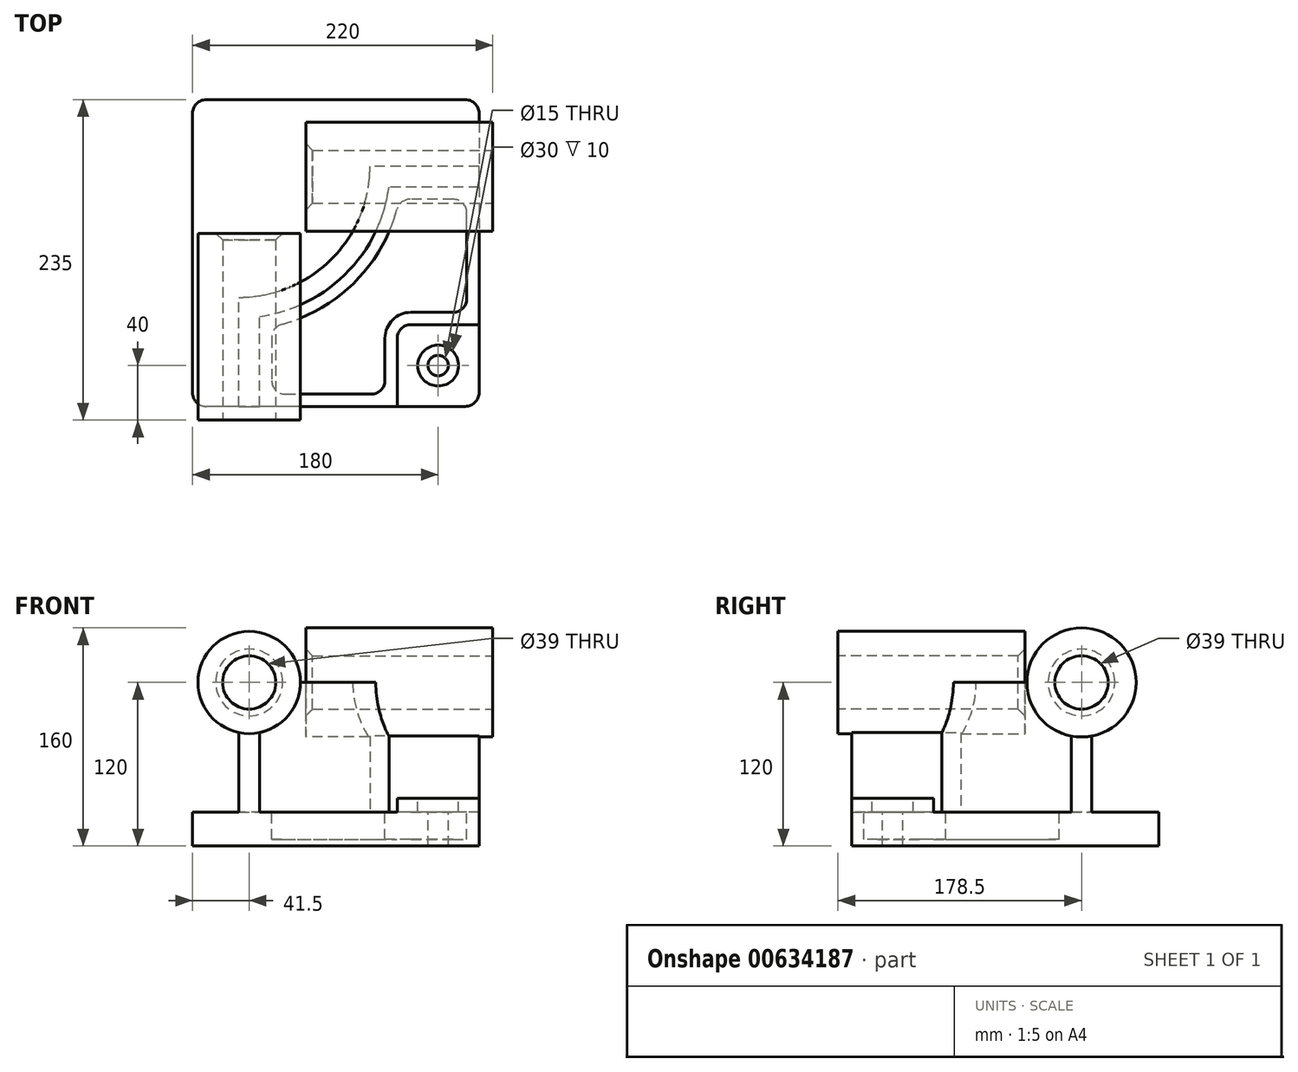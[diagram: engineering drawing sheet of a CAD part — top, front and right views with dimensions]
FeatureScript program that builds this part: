
annotation { "Feature Type Name" : "Feature", "Feature Type Description" : "" }
export const myFeature = defineFeature(function(context is Context, id is Id, definition is map)
    precondition{}
    {
        {
            var Q0;
            Q0=qCreatedBy(makeId("Top.planeOp"),FACE);
            var sketch = newSketch(context, id + "F0", { "sketchPlane" : qUnion([Q0])});
            skLineSegment(sketch, "E0.bottom", {"start": v(105, 112.5) * mm, "end": v(-105, 112.5) * mm});
            skLineSegment(sketch, "E0.top", {"start": v(105, -112.5) * mm, "end": v(-105, -112.5) * mm});
            skLineSegment(sketch, "E0.left", {"start": v(105, 112.5) * mm, "end": v(105, -112.5) * mm});
            skLineSegment(sketch, "E0.right", {"start": v(-105, 112.5) * mm, "end": v(-105, -112.5) * mm});
            skPoint(sketch, "E0.middle", {"position": v(0, 0) * mm});
            skSolve(sketch);
        }
        {
            var Q0;
            Q0=makeQuery(id+"F0.imprint","IMPRINT",FACE,{"disambiguationData":[TD([[makeQuery(id+"F0.imprint","IMPRINT",EDGE,{"derivedFrom":sQuery(id+"F0.wireOp",EDGE,"E0.bottom")}),1.0]])]});
            extrude(context, id + "F1", {"entities" : qUnion([Q0]), "depth" : 25 * mm, "offsetDistance" : 25 * mm});
        }
        {
            var Q0;
            Q0=makeQuery(id+"F1.opExtrude","CAP_FACE",FACE,{"disambiguationData":[OSD([sQuery(id+"F0.wireOp",EDGE,"E0.bottom"),sQuery(id+"F0.wireOp",EDGE,"E0.top"),sQuery(id+"F0.wireOp",EDGE,"E0.left"),sQuery(id+"F0.wireOp",EDGE,"E0.right")])],"isStart":false});
            var sketch = newSketch(context, id + "F2", { "sketchPlane" : qUnion([Q0])});
            skLineSegment(sketch, "E1", {"start": v(-71, -112.5) * mm, "end": v(-71, -32.5) * mm});
            skLineSegment(sketch, "E2", {"start": v(105, 63.5) * mm, "end": v(25, 63.5) * mm});
            skArc(sketch, "E3", {"start": v(-71, -32.5) * mm, "mid": v(-3.12, -4.38) * mm, "end": v(25, 63.5) * mm});
            skLineSegment(sketch, "E4", {"start": v(-71, 63.5) * mm, "end": v(25, 63.5) * mm, "construction": true});
            skLineSegment(sketch, "E5", {"start": v(-71, 63.5) * mm, "end": v(-71, -32.5) * mm, "construction": true});
            skLineSegment(sketch, "E6.0", {"start": v(-56, -112.5) * mm, "end": v(-56, -46.48) * mm});
            skArc(sketch, "E6.1", {"start": v(-56, -46.48) * mm, "mid": v(7.49, -14.99) * mm, "end": v(38.98, 48.5) * mm});
            skLineSegment(sketch, "E6.2", {"start": v(105, 48.5) * mm, "end": v(38.98, 48.5) * mm});
            skSolve(sketch);
        }
        {
            var Q0;
            {var subQ4=sQuery(id+"F2.wireOp",EDGE,"E1");Q0=makeQuery(id+"F2.imprint","IMPRINT",FACE,{"disambiguationData":[TD([[makeQuery(id+"F2.imprint","IMPRINT",EDGE,{"derivedFrom":subQ4}),-1.0]])]});}
            extrude(context, id + "F3", {"entities" : qUnion([Q0]), "operationType" : NewBodyOperationType.ADD, "depth" : 95 * mm, "offsetDistance" : 25 * mm});
        }
        {
            var Q0;
            {var subQ0=sQuery(id+"F0.wireOp",EDGE,"E0.top");Q0=makeQuery(id+"F3.boolean.opBoolean","MERGE",FACE,{"derivedFrom":[makeQuery(id+"F1.opExtrude","SWEPT_FACE",FACE,{"disambiguationData":[OSD([subQ0])]}),makeQuery(id+"F3.opExtrude","SWEPT_FACE",FACE,{"disambiguationData":[OSD([subQ0])]})]});}
            var sketch = newSketch(context, id + "F4", { "sketchPlane" : qUnion([Q0])});
            skCircle(sketch, "E7", {"center": v(-63.5, 120) * mm, "radius": 37.5 * mm});
            skSolve(sketch);
        }
        {
            var Q0;
            Q0 = qSketchRegion(id + "F4", true);
            extrude(context, id + "F5", {"entities" : qUnion([Q0]), "operationType" : NewBodyOperationType.ADD, "depth" : 10 * mm, "offsetDistance" : 25 * mm, "hasSecondDirection" : true, "secondDirectionOppositeDirection" : true, "secondDirectionDepth" : (137 - 10) * mm});
        }
        {
            var Q0;
            {var subQ0=sQuery(id+"F0.wireOp",EDGE,"E0.left");Q0=makeQuery(id+"F3.boolean.opBoolean","MERGE",FACE,{"derivedFrom":[makeQuery(id+"F1.opExtrude","SWEPT_FACE",FACE,{"disambiguationData":[OSD([subQ0])]}),makeQuery(id+"F3.opExtrude","SWEPT_FACE",FACE,{"disambiguationData":[OSD([subQ0])]})]});}
            var sketch = newSketch(context, id + "F6", { "sketchPlane" : qUnion([Q0])});
            skCircle(sketch, "E8", {"center": v(56, 120) * mm, "radius": 40 * mm});
            skSolve(sketch);
        }
        {
            var Q0;
            Q0 = qSketchRegion(id + "F6", true);
            extrude(context, id + "F7", {"entities" : qUnion([Q0]), "operationType" : NewBodyOperationType.ADD, "depth" : 10 * mm, "offsetDistance" : 25 * mm, "hasSecondDirection" : true, "secondDirectionOppositeDirection" : true, "secondDirectionDepth" : (137 - 10) * mm});
        }
        {
            var Q0;
            {var subQ0=sQuery(id+"F0.wireOp",EDGE,"E0.left");var subQ1=sQuery(id+"F0.wireOp",EDGE,"E0.top");Q0=makeQuery(id+"F3.boolean.opBoolean","SPLIT",FACE,{"disambiguationData":[TD([makeQuery(id+"F3.opExtrude","SWEPT_FACE",FACE,{"disambiguationData":[OSD([sQuery(id+"F2.wireOp",EDGE,"E6.0")])]})])],"derivedFrom":makeQuery(id+"F1.opExtrude","CAP_FACE",FACE,{"disambiguationData":[OSD([sQuery(id+"F0.wireOp",EDGE,"E0.bottom"),subQ1,subQ0,sQuery(id+"F0.wireOp",EDGE,"E0.right")])],"isStart":false})});}
            var sketch = newSketch(context, id + "F8", { "sketchPlane" : qUnion([Q0])});
            skLineSegment(sketch, "E9.bottom", {"start": v(105, -112.5) * mm, "end": v(45, -112.5) * mm});
            skLineSegment(sketch, "E9.top", {"start": v(105, -52.5) * mm, "end": v(45, -52.5) * mm});
            skLineSegment(sketch, "E9.left", {"start": v(105, -112.5) * mm, "end": v(105, -52.5) * mm});
            skLineSegment(sketch, "E9.right", {"start": v(45, -112.5) * mm, "end": v(45, -52.5) * mm});
            skSolve(sketch);
        }
        {
            var Q0;
            Q0 = qSketchRegion(id + "F8", true);
            extrude(context, id + "F9", {"entities" : qUnion([Q0]), "operationType" : NewBodyOperationType.ADD, "depth" : 10 * mm, "offsetDistance" : 25 * mm});
        }
        {
            var Q0;
            Q0=makeQuery(id+"F9.opExtrude","SWEPT_EDGE",EDGE,{"disambiguationData":[OSD([sQuery(id+"F8.wireOp",EDGE,"E9.top"),sQuery(id+"F8.wireOp",EDGE,"E9.right")])]});
            fillet(context, id + "F10", {"entities" : qUnion([Q0]), "radius" : 10 * mm, "tangentPropagation" : true, "allowEdgeOverflow" : false});
        }
        {
            var Q0;
            {var subQ0=sQuery(id+"F0.wireOp",EDGE,"E0.left");var subQ1=sQuery(id+"F0.wireOp",EDGE,"E0.top");Q0=makeQuery(id+"F3.boolean.opBoolean","SPLIT",FACE,{"disambiguationData":[TD([makeQuery(id+"F3.opExtrude","SWEPT_FACE",FACE,{"disambiguationData":[OSD([sQuery(id+"F2.wireOp",EDGE,"E6.0")])]})])],"derivedFrom":makeQuery(id+"F1.opExtrude","CAP_FACE",FACE,{"disambiguationData":[OSD([sQuery(id+"F0.wireOp",EDGE,"E0.bottom"),subQ1,subQ0,sQuery(id+"F0.wireOp",EDGE,"E0.right")])],"isStart":false})});}
            var sketch = newSketch(context, id + "F11", { "sketchPlane" : qUnion([Q0])});
            skLineSegment(sketch, "E10.0", {"start": v(-47, -54.08) * mm, "end": v(-47, -103.5) * mm});
            skArc(sketch, "E10.1", {"start": v(46.58, 39.5) * mm, "mid": v(13.85, -21.35) * mm, "end": v(-47, -54.08) * mm});
            skLineSegment(sketch, "E10.2", {"start": v(-47, -103.5) * mm, "end": v(36, -103.5) * mm});
            skLineSegment(sketch, "E10.3", {"start": v(96, 39.5) * mm, "end": v(46.58, 39.5) * mm});
            skLineSegment(sketch, "E10.4", {"start": v(36, -103.5) * mm, "end": v(36, -62.5) * mm});
            skArc(sketch, "E10.5", {"start": v(36, -62.5) * mm, "mid": v(41.56, -49.06) * mm, "end": v(55, -43.5) * mm});
            skLineSegment(sketch, "E10.6", {"start": v(55, -43.5) * mm, "end": v(96, -43.5) * mm});
            skLineSegment(sketch, "E10.7", {"start": v(96, -43.5) * mm, "end": v(96, 39.5) * mm});
            skSolve(sketch);
        }
        {
            var Q0;
            Q0 = qSketchRegion(id + "F11", true);
            extrude(context, id + "F12", {"entities" : qUnion([Q0]), "operationType" : NewBodyOperationType.REMOVE, "oppositeDirection" : true, "depth" : (25 - 5) * mm, "offsetDistance" : 25 * mm});
        }
        {
            var Q0;
            Q0=makeQuery(id+"F9.opExtrude","CAP_FACE",FACE,{"disambiguationData":[OSD([sQuery(id+"F8.wireOp",EDGE,"E9.bottom"),sQuery(id+"F8.wireOp",EDGE,"E9.top"),sQuery(id+"F8.wireOp",EDGE,"E9.left"),sQuery(id+"F8.wireOp",EDGE,"E9.right")])],"isStart":false});
            var sketch = newSketch(context, id + "F13", { "sketchPlane" : qUnion([Q0])});
            skCircle(sketch, "E11", {"center": v(75, -82.5) * mm, "radius": 15 * mm});
            skSolve(sketch);
        }
        {
            var Q0;
            Q0=sQuery(id+"F13.wireOp",VERTEX,"E11.center");
            var Q1;
            Q1=makeQuery(id+"F1.opExtrude","SWEPT_BODY",BODY,{"disambiguationData":[OSD([sQuery(id+"F0.wireOp",EDGE,"E0.bottom"),sQuery(id+"F0.wireOp",EDGE,"E0.top"),sQuery(id+"F0.wireOp",EDGE,"E0.left"),sQuery(id+"F0.wireOp",EDGE,"E0.right")])]});
            hole(context, id + "F14", {"style" : HoleStyle.C_BORE, "endStyle" : HoleEndStyle.THROUGH, "holeDiameter" : 15 * mm, "cBoreDiameter" : 30 * mm, "cBoreDepth" : 10 * mm, "majorDiameter" : 6.35 * mm, "isTappedThrough" : true, "tappedDepth" : 12 * mm, "tapClearance" : 3, "locations" : qUnion([Q0]), "scope" : qUnion([Q1])});
        }
        {
            var Q0;
            Q0=makeQuery(id+"F12.boolean.opBoolean","COPY",EDGE,{"derivedFrom":makeQuery(id+"F12.opExtrude","SWEPT_EDGE",EDGE,{"disambiguationData":[OSD([sQuery(id+"F11.wireOp",EDGE,"E10.0"),sQuery(id+"F11.wireOp",EDGE,"E10.1")])]})});
            var Q1;
            Q1=makeQuery(id+"F12.boolean.opBoolean","COPY",EDGE,{"derivedFrom":makeQuery(id+"F12.opExtrude","SWEPT_EDGE",EDGE,{"disambiguationData":[OSD([sQuery(id+"F11.wireOp",EDGE,"E10.1"),sQuery(id+"F11.wireOp",EDGE,"E10.3")])]})});
            var Q2;
            Q2=makeQuery(id+"F12.boolean.opBoolean","COPY",EDGE,{"derivedFrom":makeQuery(id+"F12.opExtrude","SWEPT_EDGE",EDGE,{"disambiguationData":[OSD([sQuery(id+"F11.wireOp",EDGE,"E10.3"),sQuery(id+"F11.wireOp",EDGE,"E10.7")])]})});
            var Q3;
            Q3=makeQuery(id+"F12.boolean.opBoolean","COPY",EDGE,{"derivedFrom":makeQuery(id+"F12.opExtrude","SWEPT_EDGE",EDGE,{"disambiguationData":[OSD([sQuery(id+"F11.wireOp",EDGE,"E10.6"),sQuery(id+"F11.wireOp",EDGE,"E10.7")])]})});
            var Q4;
            Q4=makeQuery(id+"F12.boolean.opBoolean","COPY",EDGE,{"derivedFrom":makeQuery(id+"F12.opExtrude","SWEPT_EDGE",EDGE,{"disambiguationData":[OSD([sQuery(id+"F11.wireOp",EDGE,"E10.2"),sQuery(id+"F11.wireOp",EDGE,"E10.4")])]})});
            var Q5;
            Q5=makeQuery(id+"F12.boolean.opBoolean","COPY",EDGE,{"derivedFrom":makeQuery(id+"F12.opExtrude","SWEPT_EDGE",EDGE,{"disambiguationData":[OSD([sQuery(id+"F11.wireOp",EDGE,"E10.0"),sQuery(id+"F11.wireOp",EDGE,"E10.2")])]})});
            fillet(context, id + "F15", {"entities" : qUnion([Q0, Q1, Q2, Q3, Q4, Q5]), "radius" : 10 * mm, "tangentPropagation" : true, "allowEdgeOverflow" : false});
        }
        {
            var Q0;
            Q0=makeQuery(id+"F5.opExtrude","CAP_FACE",FACE,{"disambiguationData":[OSD([sQuery(id+"F4.wireOp",EDGE,"E7")])],"isStart":false});
            var sketch = newSketch(context, id + "F16", { "sketchPlane" : qUnion([Q0])});
            skCircle(sketch, "E12", {"center": v(-63.5, 120) * mm, "radius": 19.5 * mm});
            skSolve(sketch);
        }
        {
            var Q0;
            Q0 = qSketchRegion(id + "F16", true);
            extrude(context, id + "F17", {"entities" : qUnion([Q0]), "operationType" : NewBodyOperationType.REMOVE, "endBound" : BoundingType.THROUGH_ALL, "oppositeDirection" : true, "depth" : 25 * mm, "offsetDistance" : 25 * mm});
        }
        {
            var Q0;
            Q0=makeQuery(id+"F7.opExtrude","CAP_FACE",FACE,{"disambiguationData":[OSD([sQuery(id+"F6.wireOp",EDGE,"E8")])],"isStart":false});
            var sketch = newSketch(context, id + "F18", { "sketchPlane" : qUnion([Q0])});
            skCircle(sketch, "E13", {"center": v(56, 120) * mm, "radius": 19.5 * mm});
            skSolve(sketch);
        }
        {
            var Q0;
            Q0 = qSketchRegion(id + "F18", true);
            extrude(context, id + "F19", {"entities" : qUnion([Q0]), "operationType" : NewBodyOperationType.REMOVE, "endBound" : BoundingType.THROUGH_ALL, "oppositeDirection" : true, "depth" : 25 * mm, "offsetDistance" : 25 * mm});
        }
        {
            var Q0;
            Q0=makeQuery(id+"F19.boolean.opBoolean","COPY",EDGE,{"derivedFrom":makeQuery(id+"F19.opExtrude","CAP_EDGE",EDGE,{"disambiguationData":[OSD([sQuery(id+"F18.wireOp",EDGE,"E13")])],"isStart":true})});
            var Q1;
            Q1=makeQuery(id+"F19.boolean.opBoolean","INTERSECT",EDGE,{"derivedFrom":[makeQuery(id+"F7.opExtrude","CAP_FACE",FACE,{"disambiguationData":[OSD([sQuery(id+"F6.wireOp",EDGE,"E8")])],"isStart":true}),makeQuery(id+"F19.opExtrude","SWEPT_FACE",FACE,{"disambiguationData":[OSD([sQuery(id+"F18.wireOp",EDGE,"E13")])]})]});
            var Q2;
            Q2=makeQuery(id+"F17.boolean.opBoolean","INTERSECT",EDGE,{"derivedFrom":[makeQuery(id+"F5.opExtrude","CAP_FACE",FACE,{"disambiguationData":[OSD([sQuery(id+"F4.wireOp",EDGE,"E7")])],"isStart":true}),makeQuery(id+"F17.opExtrude","SWEPT_FACE",FACE,{"disambiguationData":[OSD([sQuery(id+"F16.wireOp",EDGE,"E12")])]})]});
            var Q3;
            Q3=makeQuery(id+"F17.boolean.opBoolean","COPY",EDGE,{"derivedFrom":makeQuery(id+"F17.opExtrude","CAP_EDGE",EDGE,{"disambiguationData":[OSD([sQuery(id+"F16.wireOp",EDGE,"E12")])],"isStart":true})});
            chamfer(context, id + "F20", {"entities" : qUnion([Q0, Q1, Q2, Q3]), "width" : 5 * mm, "tangentPropagation" : true});
        }
        {
            var Q0;
            Q0=makeQuery(id+"F1.opExtrude","SWEPT_EDGE",EDGE,{"disambiguationData":[OSD([sQuery(id+"F0.wireOp",EDGE,"E0.top"),sQuery(id+"F0.wireOp",EDGE,"E0.right")])]});
            var Q1;
            Q1=makeQuery(id+"F9.boolean.opBoolean","MERGE",EDGE,{"derivedFrom":[makeQuery(id+"F1.opExtrude","SWEPT_EDGE",EDGE,{"disambiguationData":[OSD([sQuery(id+"F0.wireOp",EDGE,"E0.top"),sQuery(id+"F0.wireOp",EDGE,"E0.left")])]}),makeQuery(id+"F9.opExtrude","SWEPT_EDGE",EDGE,{"disambiguationData":[OSD([sQuery(id+"F8.wireOp",EDGE,"E9.bottom"),sQuery(id+"F8.wireOp",EDGE,"E9.left")])]})]});
            var Q2;
            Q2=makeQuery(id+"F1.opExtrude","SWEPT_EDGE",EDGE,{"disambiguationData":[OSD([sQuery(id+"F0.wireOp",EDGE,"E0.bottom"),sQuery(id+"F0.wireOp",EDGE,"E0.left")])]});
            var Q3;
            Q3=makeQuery(id+"F1.opExtrude","SWEPT_EDGE",EDGE,{"disambiguationData":[OSD([sQuery(id+"F0.wireOp",EDGE,"E0.bottom"),sQuery(id+"F0.wireOp",EDGE,"E0.right")])]});
            fillet(context, id + "F21", {"entities" : qUnion([Q0, Q1, Q2, Q3]), "radius" : 10 * mm, "tangentPropagation" : true, "allowEdgeOverflow" : false});
        }
    });
